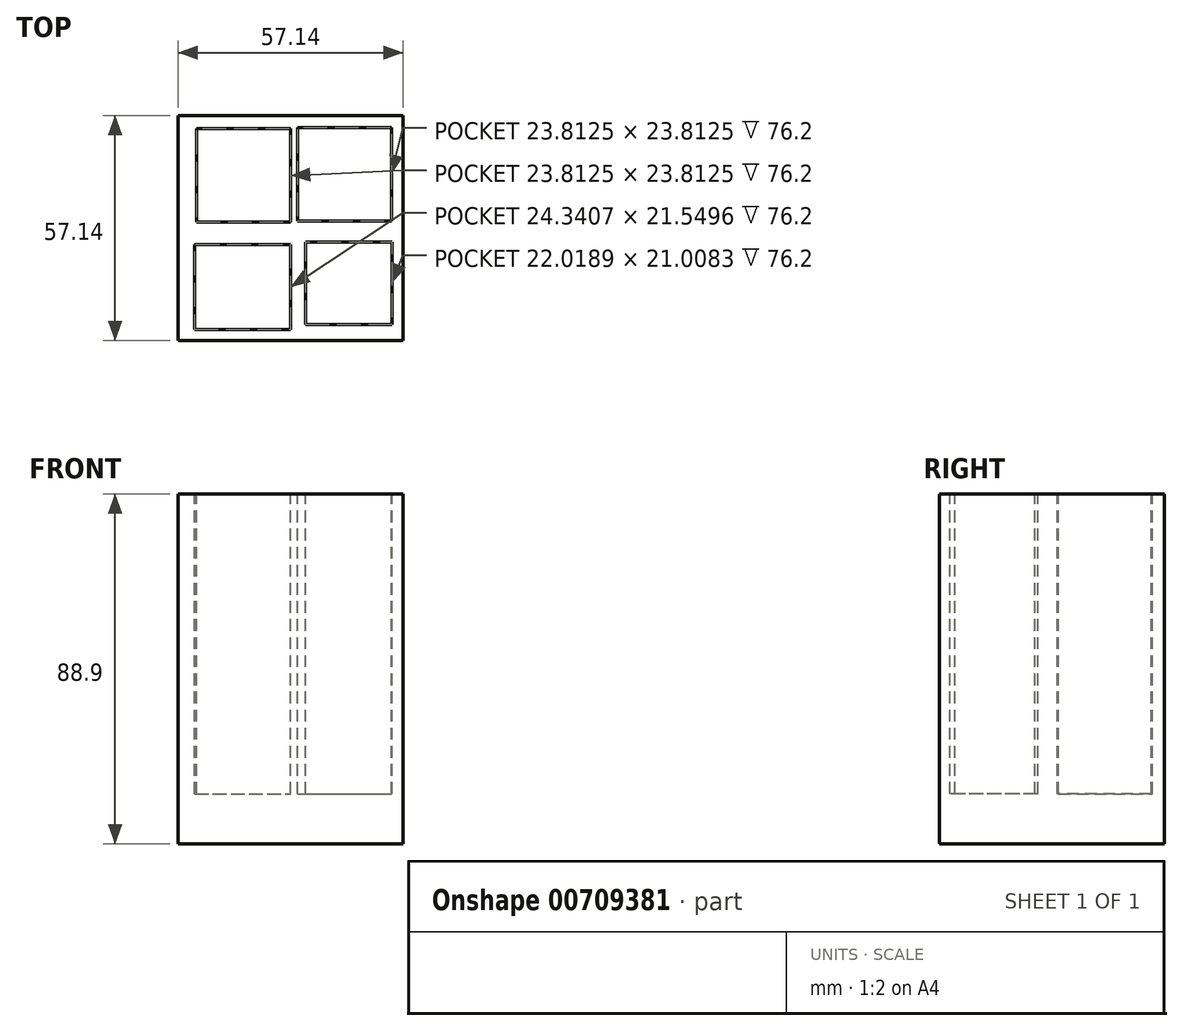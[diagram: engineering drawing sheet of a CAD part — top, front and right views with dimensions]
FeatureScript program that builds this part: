
annotation { "Feature Type Name" : "Feature", "Feature Type Description" : "" }
export const myFeature = defineFeature(function(context is Context, id is Id, definition is map)
    precondition{}
    {
        {
            var Q0;
            Q0=qCreatedBy(makeId("Top.planeOp"),FACE);
            var sketch = newSketch(context, id + "F0", { "sketchPlane" : qUnion([Q0])});
            skLineSegment(sketch, "E0.bottom", {"start": v(-28.57, 28.58) * mm, "end": v(28.58, 28.58) * mm});
            skLineSegment(sketch, "E0.top", {"start": v(-28.58, -28.58) * mm, "end": v(28.57, -28.58) * mm});
            skLineSegment(sketch, "E0.left", {"start": v(-28.57, 28.58) * mm, "end": v(-28.58, -28.58) * mm});
            skLineSegment(sketch, "E0.right", {"start": v(28.58, 28.58) * mm, "end": v(28.57, -28.58) * mm});
            skPoint(sketch, "E0.middle", {"position": v(0, 0) * mm});
            skSolve(sketch);
        }
        {
            var Q0;
            Q0 = qSketchRegion(id + "F0", true);
            extrude(context, id + "F1", {"entities" : qUnion([Q0]), "depth" : 88.9 * mm, "offsetDistance" : 25.4 * mm});
        }
        {
            var Q0;
            Q0=makeQuery(id+"F1.opExtrude","CAP_FACE",FACE,{"disambiguationData":[OSD([sQuery(id+"F0.wireOp",EDGE,"E0.bottom"),sQuery(id+"F0.wireOp",EDGE,"E0.top"),sQuery(id+"F0.wireOp",EDGE,"E0.left"),sQuery(id+"F0.wireOp",EDGE,"E0.right")])],"isStart":false});
            var sketch = newSketch(context, id + "F2", { "sketchPlane" : qUnion([Q0])});
            skLineSegment(sketch, "E1.bottom", {"start": v(1.82, 1.75) * mm, "end": v(25.63, 1.75) * mm});
            skLineSegment(sketch, "E1.top", {"start": v(1.82, 25.56) * mm, "end": v(25.63, 25.56) * mm});
            skLineSegment(sketch, "E1.left", {"start": v(1.82, 1.75) * mm, "end": v(1.82, 25.56) * mm});
            skLineSegment(sketch, "E1.right", {"start": v(25.63, 1.75) * mm, "end": v(25.63, 25.56) * mm});
            skSolve(sketch);
        }
        {
            var Q0;
            Q0 = qSketchRegion(id + "F2", true);
            extrude(context, id + "F3", {"entities" : qUnion([Q0]), "operationType" : NewBodyOperationType.REMOVE, "oppositeDirection" : true, "depth" : 76.2 * mm, "offsetDistance" : 25.4 * mm});
        }
        {
            var Q0;
            Q0=makeQuery(id+"F1.opExtrude","CAP_FACE",FACE,{"disambiguationData":[OSD([sQuery(id+"F0.wireOp",EDGE,"E0.bottom"),sQuery(id+"F0.wireOp",EDGE,"E0.top"),sQuery(id+"F0.wireOp",EDGE,"E0.left"),sQuery(id+"F0.wireOp",EDGE,"E0.right")])],"isStart":false});
            var sketch = newSketch(context, id + "F4", { "sketchPlane" : qUnion([Q0])});
            skLineSegment(sketch, "E2.bottom", {"start": v(-23.84, 25.28) * mm, "end": v(-0.03, 25.28) * mm});
            skLineSegment(sketch, "E2.top", {"start": v(-23.84, 1.47) * mm, "end": v(-0.03, 1.47) * mm});
            skLineSegment(sketch, "E2.left", {"start": v(-23.84, 25.28) * mm, "end": v(-23.84, 1.47) * mm});
            skLineSegment(sketch, "E2.right", {"start": v(-0.03, 25.28) * mm, "end": v(-0.03, 1.47) * mm});
            skSolve(sketch);
        }
        {
            var Q0;
            Q0 = qSketchRegion(id + "F4", true);
            extrude(context, id + "F5", {"entities" : qUnion([Q0]), "operationType" : NewBodyOperationType.REMOVE, "oppositeDirection" : true, "depth" : 76.2 * mm, "offsetDistance" : 25.4 * mm});
        }
        {
            var Q0;
            Q0=makeQuery(id+"F1.opExtrude","CAP_FACE",FACE,{"disambiguationData":[OSD([sQuery(id+"F0.wireOp",EDGE,"E0.bottom"),sQuery(id+"F0.wireOp",EDGE,"E0.top"),sQuery(id+"F0.wireOp",EDGE,"E0.left"),sQuery(id+"F0.wireOp",EDGE,"E0.right")])],"isStart":false});
            var sketch = newSketch(context, id + "F6", { "sketchPlane" : qUnion([Q0])});
            skLineSegment(sketch, "E3.bottom", {"start": v(-24.34, -4.24) * mm, "end": v(0, -4.24) * mm});
            skLineSegment(sketch, "E3.top", {"start": v(-24.34, -25.8) * mm, "end": v(0, -25.8) * mm});
            skLineSegment(sketch, "E3.left", {"start": v(-24.34, -4.24) * mm, "end": v(-24.34, -25.8) * mm});
            skLineSegment(sketch, "E3.right", {"start": v(0, -4.24) * mm, "end": v(0, -25.8) * mm});
            skSolve(sketch);
        }
        {
            var Q0;
            Q0 = qSketchRegion(id + "F6", true);
            extrude(context, id + "F7", {"entities" : qUnion([Q0]), "operationType" : NewBodyOperationType.REMOVE, "oppositeDirection" : true, "depth" : 76.2 * mm, "offsetDistance" : 25.4 * mm});
        }
        {
            var Q0;
            Q0=makeQuery(id+"F1.opExtrude","CAP_FACE",FACE,{"disambiguationData":[OSD([sQuery(id+"F0.wireOp",EDGE,"E0.bottom"),sQuery(id+"F0.wireOp",EDGE,"E0.top"),sQuery(id+"F0.wireOp",EDGE,"E0.left"),sQuery(id+"F0.wireOp",EDGE,"E0.right")])],"isStart":false});
            var sketch = newSketch(context, id + "F8", { "sketchPlane" : qUnion([Q0])});
            skLineSegment(sketch, "E4.bottom", {"start": v(3.78, -3.53) * mm, "end": v(25.8, -3.53) * mm});
            skLineSegment(sketch, "E4.top", {"start": v(3.78, -24.54) * mm, "end": v(25.8, -24.54) * mm});
            skLineSegment(sketch, "E4.left", {"start": v(3.78, -3.53) * mm, "end": v(3.78, -24.54) * mm});
            skLineSegment(sketch, "E4.right", {"start": v(25.8, -3.53) * mm, "end": v(25.8, -24.54) * mm});
            skSolve(sketch);
        }
        {
            var Q0;
            Q0 = qSketchRegion(id + "F8", true);
            extrude(context, id + "F9", {"entities" : qUnion([Q0]), "operationType" : NewBodyOperationType.REMOVE, "oppositeDirection" : true, "depth" : 76.2 * mm, "offsetDistance" : 25.4 * mm});
        }
    });
